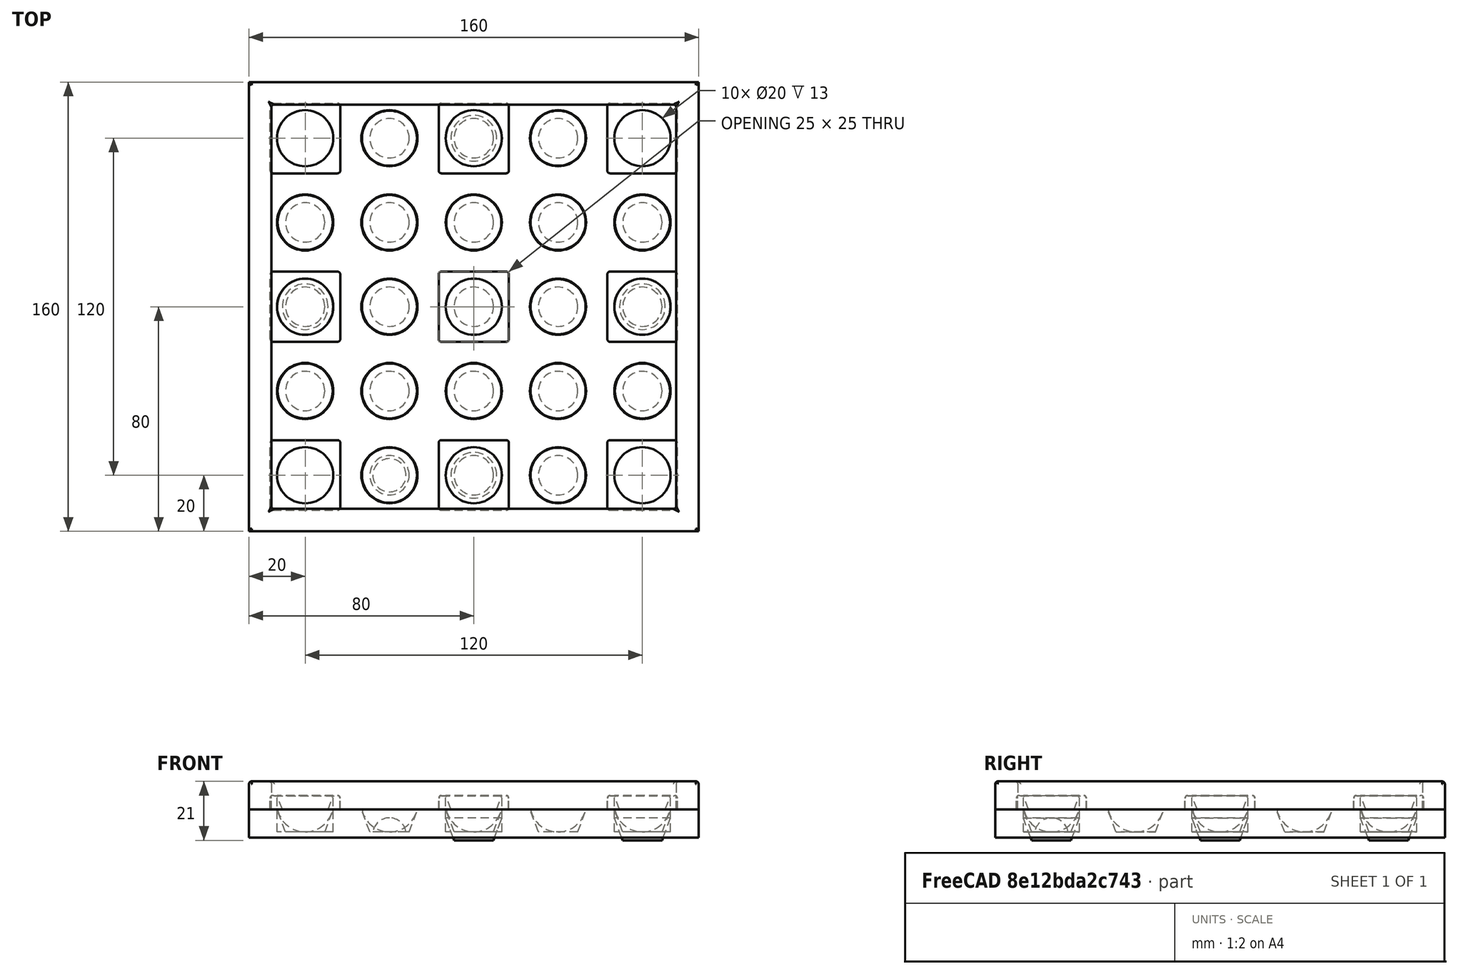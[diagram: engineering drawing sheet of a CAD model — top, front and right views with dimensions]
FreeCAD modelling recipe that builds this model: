
FCSTD DOCUMENT  (FreeCAD 0.16R6712 (Git))
Label: diseño tablero
License: All rights reserved
LicenseURL: http://en.wikipedia.org/wiki/All_rights_reserved
objects: Part::FeaturePython×11, Part::Fillet×7, Part::Fuse×7, Part::Cut×6, Part::Box×4, Part::Cone×3, Part::Sphere×2, Part::Cylinder×2
note: 42 computed .brp shape members not serialized (recipe doc carries the construction recipe); baked Part::Feature solids carry a one-line shape summary decoded from their .brp

FEATURE [Part::Box] Box  label="base"
  Height = 10
  Length = 160
  Width = 160
FEATURE [Part::Sphere] Sphere  label="esfera"
  Angle1 = -90
  Angle2 = 90
  Angle3 = 360
  Placement = pos=(20,20,12) rot=(0,0,1;0rad)
  Radius = 10
FEATURE [Part::FeaturePython] Array  label="esferas"  # Draft array (typed FeaturePython)
  Angle = 360
  ArrayType = 0
  Axis = (0,0,1)
  Base = -> Sphere
  Center = (0,0,0)
  Fuse = false
  IntervalAxis = (0,0,0)
  IntervalX = (30,0,0)
  IntervalY = (0,30,0)
  IntervalZ = (0,0,0)
  NumberPolar = 1
  NumberX = 5
  NumberY = 5
  NumberZ = 1
FEATURE [Part::Cut] Cut  label="tableroAgujereado"
  Base = -> Box
  Tool = -> Array
FEATURE [Part::Cylinder] Cylinder  label="madriguera"
  Angle = 360
  Height = 20
  Placement = pos=(20,20,2) rot=(0,0,1;0rad)
  Radius = 10
FEATURE [Part::FeaturePython] Array001  label="madrigueras"  # Draft array (typed FeaturePython)
  Angle = 360
  ArrayType = 0
  Axis = (0,0,1)
  Base = -> Cylinder
  Center = (0,0,0)
  Fuse = false
  IntervalAxis = (0,0,0)
  IntervalX = (120,0,0)
  IntervalY = (0,120,0)
  IntervalZ = (0,0,0)
  NumberPolar = 1
  NumberX = 2
  NumberY = 2
  NumberZ = 1
FEATURE [Part::Box] Box001  label="bordeMadriguera"
  Height = 5
  Length = 25
  Placement = pos=(7.5,7.5,10) rot=(0,0,1;0rad)
  Width = 25
FEATURE [Part::Fillet] Fillet  label="saliente Redondeado"
  Base = -> Box001
  Edges = 8 edges r=1: [Edge1,Edge2,Edge3,Edge5,Edge6,Edge7,Edge10,Edge12]
FEATURE [Part::FeaturePython] Array002  label="salientes"  # Draft array (typed FeaturePython)
  Angle = 360
  ArrayType = 0
  Axis = (0,0,1)
  Base = -> Fillet
  Center = (0,0,0)
  Fuse = false
  IntervalAxis = (0,0,0)
  IntervalX = (60,0,0)
  IntervalY = (0,60,0)
  IntervalZ = (0,0,0)
  NumberPolar = 1
  NumberX = 3
  NumberY = 3
  NumberZ = 1
FEATURE [Part::Cylinder] Cylinder001  label="madrigueraCentro"
  Angle = 360
  Height = 20
  Placement = pos=(80,80,2) rot=(0,0,1;0rad)
  Radius = 10
FEATURE [Part::Fuse] Fusion  label="Madrigueras"
  Base = -> Array001
  Tool = -> Cylinder001
FEATURE [Part::Fuse] Fusion001  label="Tablero"
  Base = -> Cut
  Tool = -> Array002
FEATURE [Part::Cut] Cut001  label="TableroSinBordes"
  Base = -> Fusion001
  Tool = -> Fusion
FEATURE [Part::Sphere] Sphere001  label="Sphere"
  Angle1 = 10
  Angle2 = 90
  Angle3 = 360
  Placement = pos=(50,20,1) rot=(0,0,1;0rad)
  Radius = 6
FEATURE [Part::Cone] Cone
  Angle = 360
  Height = 8
  Placement = pos=(20,20,2) rot=(0,0,1;0rad)
  Radius1 = 7
  Radius2 = 10
FEATURE [Part::FeaturePython] Array003  label="conos"  # Draft array (typed FeaturePython)
  Angle = 360
  ArrayType = 0
  Axis = (0,0,1)
  Base = -> Cone
  Center = (0,0,0)
  Fuse = false
  IntervalAxis = (0,0,0)
  IntervalX = (30,0,0)
  IntervalY = (0,30,0)
  IntervalZ = (0,0,0)
  NumberPolar = 1
  NumberX = 5
  NumberY = 5
  NumberZ = 1
FEATURE [Part::Cut] Cut002  label="tableroConos"
  Base = -> Box
  Tool = -> Array003
FEATURE [Part::Fuse] Fusion002  label="tableroConSalientes"
  Base = -> Array002
  Tool = -> Cut002
FEATURE [Part::Cut] Cut003  label="TableroSinBordesConos"
  Base = -> Fusion002
  Tool = -> Fusion
FEATURE [Part::Cone] Cone001  label="Cono alto"
  Angle = 360
  Height = 8
  Placement = pos=(20,80,7) rot=(0,0,1;0rad)
  Radius1 = 7
  Radius2 = 10
FEATURE [Part::FeaturePython] Clone  label="Clone of Cono alto 2"  # Draft clone (typed FeaturePython)
  Objects = -> [Cone001]
  Placement = pos=(80,140,7) rot=(0,0,1;0rad)
  Scale = (1,1,1)
FEATURE [Part::FeaturePython] Clone001  label="Clone of Cono alto 3"  # Draft clone (typed FeaturePython)
  Objects = -> [Cone001]
  Placement = pos=(80,20,7) rot=(0,0,1;0rad)
  Scale = (1,1,1)
FEATURE [Part::FeaturePython] Clone002  label="Clone of Cono alto 4"  # Draft clone (typed FeaturePython)
  Objects = -> [Cone001]
  Placement = pos=(140,80,7) rot=(0,0,1;0rad)
  Scale = (1,1,1)
FEATURE [Part::Fuse] Fusion003
  Base = -> Cone001
  Tool = -> Clone
FEATURE [Part::Fuse] Fusion004
  Base = -> Clone001
  Tool = -> Fusion003
FEATURE [Part::Fuse] Fusion005  label="Conos Altos"
  Base = -> Clone002
  Tool = -> Fusion004
FEATURE [Part::Cut] Cut004  label="Tablero sin bordes"
  Base = -> Cut003
  Tool = -> Fusion005
FEATURE [Part::Box] Box002  label="Cube"
  Height = 10
  Length = 160
  Placement = pos=(0,0,27) rot=(0,0,1;0rad)
  Width = 160
FEATURE [Part::Box] Box003  label="Cube001"
  Height = 10
  Length = 144
  Placement = pos=(8,8,27) rot=(0,0,1;0rad)
  Width = 144
FEATURE [Part::Cut] Cut005  label="Borde"
  Base = -> Box002
  Placement = pos=(0,0,-17) rot=(0,0,1;0rad)
  Tool = -> Box003
FEATURE [Part::Fillet] Fillet001
  Base = -> Cut005
  Edges = 4 edges r=1: [Edge2,Edge7,Edge8,Edge9]
FEATURE [Part::Fillet] Fillet002
  Base = -> Fillet001
  Edges = 4 edges r=1: [Edge24,Edge25,Edge26,Edge27]
FEATURE [Part::Fillet] Fillet003
  Base = -> Fillet002
  Edges = 2 edges r=1: [Edge9,Edge27]
FEATURE [Part::Fillet] Fillet004  label="BordeExterior"
  Base = -> Fillet003
  Edges = 6 edges r=1: [Edge3,Edge6,Edge11,Edge22,Edge31,Edge41]
FEATURE [Part::Fuse] Fusion006
  Base = -> Cut004
  Tool = -> Fillet004
FEATURE [Part::Fillet] Fillet005
  Base = -> Fusion006
  Edges = 1 edges r=0.9: [Edge500]
FEATURE [Part::Fillet] Fillet006  label="Tablero bordes redondeados"
  Base = -> Fillet005
  Edges = 3 edges r=0.9: [Edge6,Edge22,Edge41]
FEATURE [Part::Cone] Cone002  label="cono tapar"
  Angle = 360
  Height = 8
  Placement = pos=(20,80,-1) rot=(0,0,1;0rad)
  Radius1 = 7
  Radius2 = 10
FEATURE [Part::FeaturePython] Clone003  label="Clone of cono tapar"  # Draft clone (typed FeaturePython)
  Objects = -> [Cone002]
  Placement = pos=(140,80,-1) rot=(0,0,1;0rad)
  Scale = (1,1,1)
FEATURE [Part::FeaturePython] Clone004  label="Clone of cono tapar001"  # Draft clone (typed FeaturePython)
  Objects = -> [Cone002]
  Placement = pos=(80,140,-1) rot=(0,0,1;0rad)
  Scale = (1,1,1)
FEATURE [Part::FeaturePython] Clone005  label="Clone of cono tapar002"  # Draft clone (typed FeaturePython)
  Objects = -> [Cone002]
  Placement = pos=(80,20,-1) rot=(0,0,1;0rad)
  Scale = (1,1,1)
FEATURE [Part::FeaturePython] Clone006  label="Clone of cono tapar003"  # Draft clone (typed FeaturePython)
  Objects = -> [Cone002]
  Placement = pos=(80,80,-1) rot=(0,0,1;0rad)
  Scale = (1,1,1)
